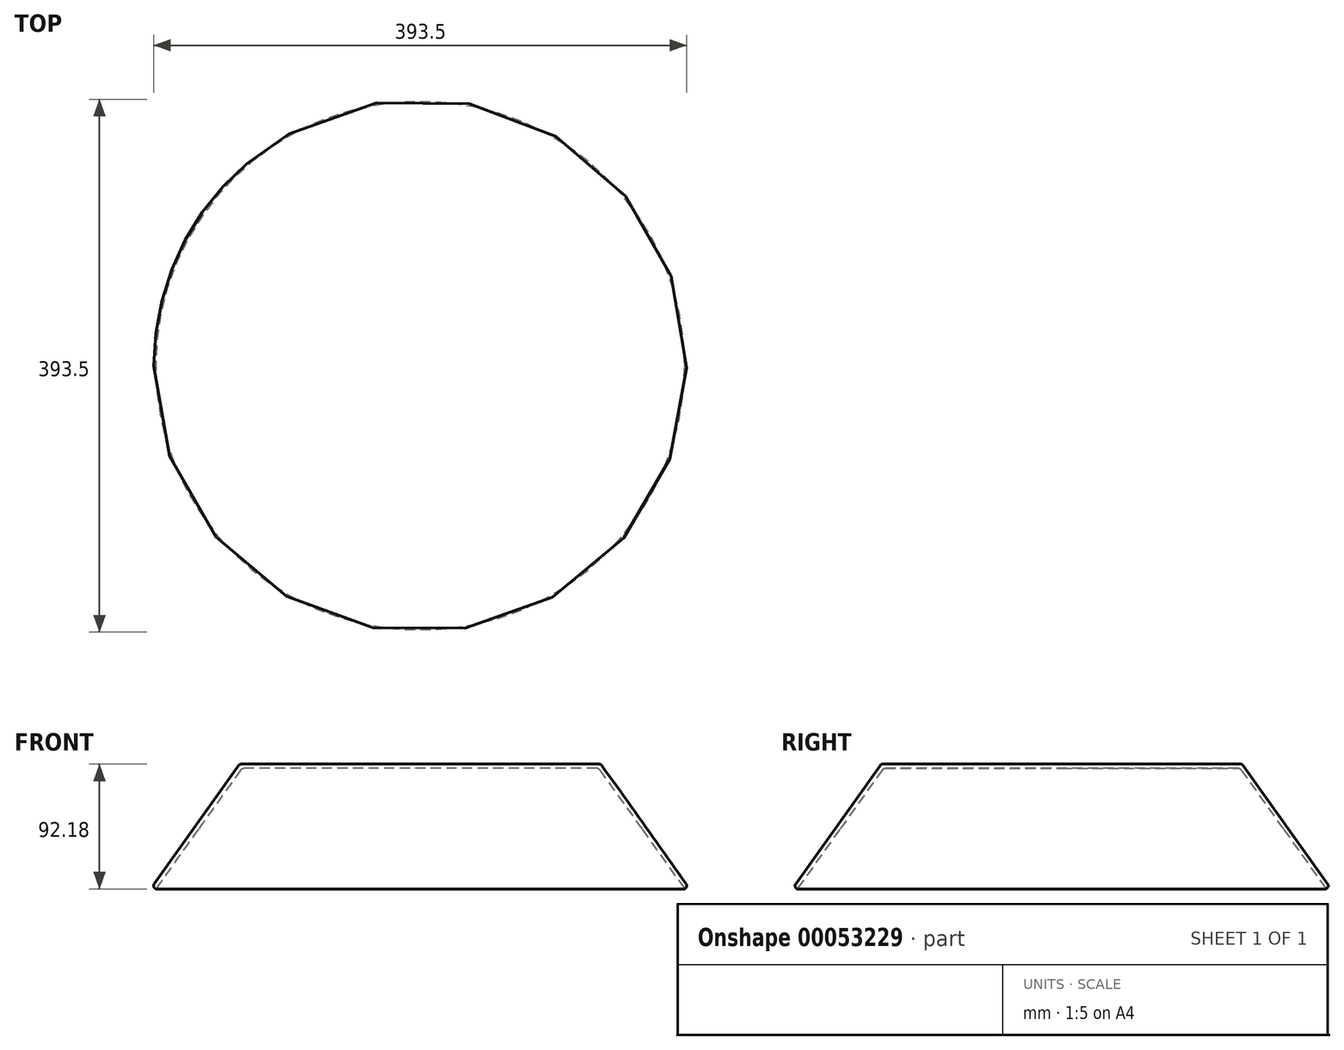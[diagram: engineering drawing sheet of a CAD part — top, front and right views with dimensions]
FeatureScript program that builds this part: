
annotation { "Feature Type Name" : "Feature", "Feature Type Description" : "" }
export const myFeature = defineFeature(function(context is Context, id is Id, definition is map)
    precondition{}
    {
        {
            var Q0;
            Q0=qCreatedBy(makeId("Right.planeOp"),FACE);
            var sketch = newSketch(context, id + "F0", { "sketchPlane" : qUnion([Q0])});
            skLineSegment(sketch, "E0", {"start": v(0, 48.26) * mm, "end": v(-133.35, 48.26) * mm});
            skLineSegment(sketch, "E1", {"start": v(-133.35, 48.26) * mm, "end": v(-198.98, -43.92) * mm});
            skLineSegment(sketch, "E2", {"start": v(-163.81, 0) * mm, "end": v(-131.71, 45.08) * mm});
            skLineSegment(sketch, "E3", {"start": v(-131.71, 45.08) * mm, "end": v(0, 45.08) * mm});
            skLineSegment(sketch, "E4", {"start": v(0, 45.08) * mm, "end": v(0, 48.26) * mm});
            skPoint(sketch, "E5.end.orphan", {"position": v(-220.32, 0) * mm});
            skPoint(sketch, "E6.end.orphan", {"position": v(-220.32, 3.18) * mm});
            skLineSegment(sketch, "E7", {"start": v(-198.98, -43.92) * mm, "end": v(-195.25, -43.92) * mm});
            skLineSegment(sketch, "E8", {"start": v(-195.25, -43.92) * mm, "end": v(-163.81, 0) * mm});
            skSolve(sketch);
        }
        {
            var Q0;
            Q0 = qSketchRegion(id + "F0", true);
            var Q1;
            Q1=sQuery(id+"F0.wireOp",EDGE,"E4");
            revolve(context, id + "F1", {"entities" : qUnion([Q0]), "axis" : qUnion([Q1]), "revolveType" : RevolveType.FULL});
        }
        {
            var Q0;
            Q0=makeQuery(id+"F1.opRevolve","SWEPT_EDGE",EDGE,{"disambiguationData":[OSD([sQuery(id+"F0.wireOp",EDGE,"E0"),sQuery(id+"F0.wireOp",EDGE,"E1")])]});
            var Q1;
            Q1=makeQuery(id+"F1.opRevolve","SWEPT_EDGE",EDGE,{"disambiguationData":[OSD([sQuery(id+"F0.wireOp",EDGE,"E1"),sQuery(id+"F0.wireOp",EDGE,"E6")])]});
            var Q2;
            Q2=makeQuery(id+"F1.opRevolve","SWEPT_EDGE",EDGE,{"disambiguationData":[OSD([sQuery(id+"F0.wireOp",EDGE,"E6"),sQuery(id+"F0.wireOp",EDGE,"E5")])]});
            fillet(context, id + "F2", {"entities" : qUnion([Q0, Q1, Q2]), "radius" : 2.54 * mm, "tangentPropagation" : true, "allowEdgeOverflow" : false});
        }
        {
            var Q0;
            Q0=makeQuery(id+"F1.opRevolve","SWEPT_EDGE",EDGE,{"disambiguationData":[OSD([sQuery(id+"F0.wireOp",EDGE,"E2"),sQuery(id+"F0.wireOp",EDGE,"E3")])]});
            var Q1;
            Q1=makeQuery(id+"F1.opRevolve","SWEPT_EDGE",EDGE,{"disambiguationData":[OSD([sQuery(id+"F0.wireOp",EDGE,"fe7e0134-3015-4715-a2ef-af61e218a45e"),sQuery(id+"F0.wireOp",EDGE,"E2")])]});
            fillet(context, id + "F3", {"entities" : qUnion([Q0, Q1]), "radius" : 2.54 * mm, "tangentPropagation" : true, "allowEdgeOverflow" : false});
        }
    });
